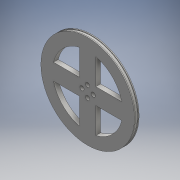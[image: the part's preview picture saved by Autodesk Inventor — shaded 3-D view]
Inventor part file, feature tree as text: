
AUTODESK INVENTOR PART (.ipt)
format: ipt  version: 2016 (Build 200138000, 138)  size: 180,224 bytes
history: native  units: mm
features: sketch x4, extrude x3, hole x1
ambient origin geometry x8: Origin, YZ Plane, XZ Plane, XY Plane, X Axis, Y Axis, Z Axis, Center Point
bodies: Solid1 (feature_tree)
feature tree (8):
  extrude  "Extrusion1"  Depth=75.0mm
  extrude  "Extrusion3"  Depth=1.0mm TaperAngle=0.0deg
  extrude  "Extrusion4"  Depth=3.0mm TaperAngle=0.0deg
  hole  "Hole2"  [1 undecoded]
  sketch  "Sketch1"  dims[d0=100.0mm d1=75.0mm]
  sketch  "Sketch6"  dims[d2=17.5mm d14=1.0mm d15=0.0mm]
  sketch  "Sketch7"  dims[d33=98.5mm d35=3.0mm d36=0.0mm]
  sketch  "Sketch8"  dims[d37=100.0mm d38=1.0mm d39=0.0mm d40=4.5mm d41=6.0mm d42=4.5mm d43=6.0mm d44=4.5mm d45=6.0mm d46=4.0mm d47=2.0mm d48=90.0deg d49=8.0mm d50=20.594885mm]
note: 1 required parameter value undecoded (feature->parameter linkage not recoverable at this tier; creation-order binding heuristic only, values carry confidence <= 0.55)
